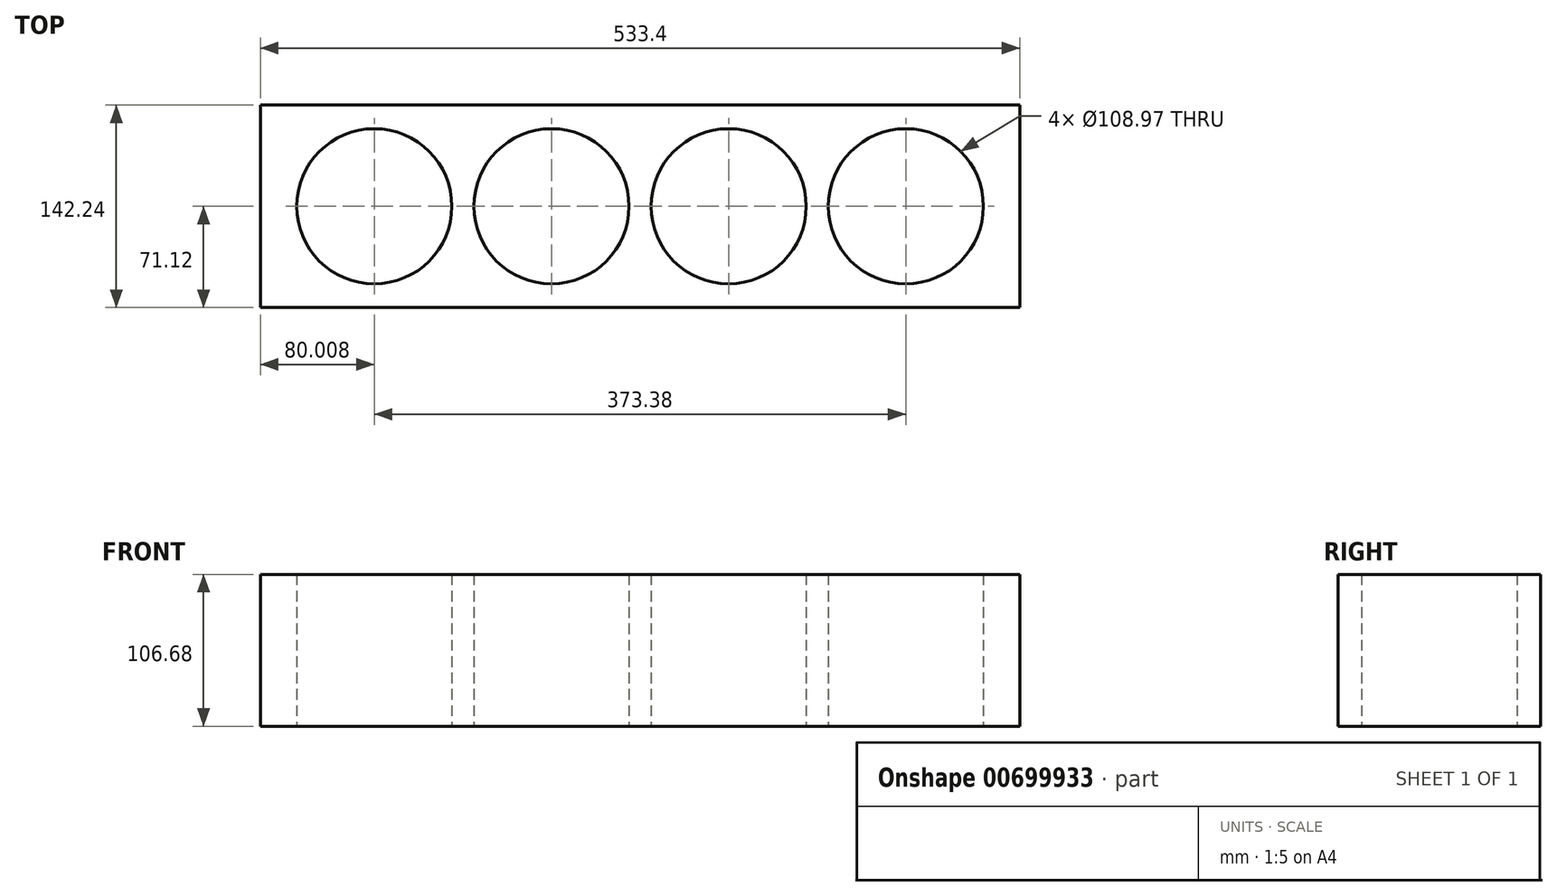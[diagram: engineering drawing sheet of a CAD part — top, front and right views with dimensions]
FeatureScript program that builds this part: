
annotation { "Feature Type Name" : "Feature", "Feature Type Description" : "" }
export const myFeature = defineFeature(function(context is Context, id is Id, definition is map)
    precondition{}
    {
        {
            var Q0;
            Q0=qCreatedBy(makeId("Top.planeOp"),FACE);
            var sketch = newSketch(context, id + "F0", { "sketchPlane" : qUnion([Q0])});
            skCircle(sketch, "E0", {"center": v(-148.3, 0) * mm, "radius": 54.48 * mm});
            skCircle(sketch, "E1.1.0.0", {"center": v(-23.84, 0) * mm, "radius": 54.48 * mm});
            skCircle(sketch, "E1.2.0.0", {"center": v(100.62, 0) * mm, "radius": 54.48 * mm});
            skCircle(sketch, "E1.3.0.0", {"center": v(225.08, 0) * mm, "radius": 54.48 * mm});
            skLineSegment(sketch, "E1.direction1", {"start": v(-148.3, 0) * mm, "end": v(-23.84, 0) * mm, "construction": true});
            skLineSegment(sketch, "E2", {"start": v(-148.3, 0) * mm, "end": v(225.08, 0) * mm, "construction": true});
            skLineSegment(sketch, "E3.bottom", {"start": v(305.09, 71.12) * mm, "end": v(-228.31, 71.12) * mm});
            skLineSegment(sketch, "E3.top", {"start": v(305.09, -71.12) * mm, "end": v(-228.31, -71.12) * mm});
            skLineSegment(sketch, "E3.left", {"start": v(305.09, 71.12) * mm, "end": v(305.09, -71.12) * mm});
            skLineSegment(sketch, "E3.right", {"start": v(-228.31, 71.12) * mm, "end": v(-228.31, -71.12) * mm});
            skPoint(sketch, "E3.middle", {"position": v(38.39, 0) * mm});
            skSolve(sketch);
        }
        {
            var Q0;
            Q0=makeQuery(id+"F0.imprint","IMPRINT",FACE,{"disambiguationData":[TD([[makeQuery(id+"F0.imprint","IMPRINT",EDGE,{"derivedFrom":sQuery(id+"F0.wireOp",EDGE,"E0")}),-1.0]])]});
            extrude(context, id + "F1", {"entities" : qUnion([Q0]), "depth" : 106.68 * mm, "offsetDistance" : 25.4 * mm});
        }
    });
